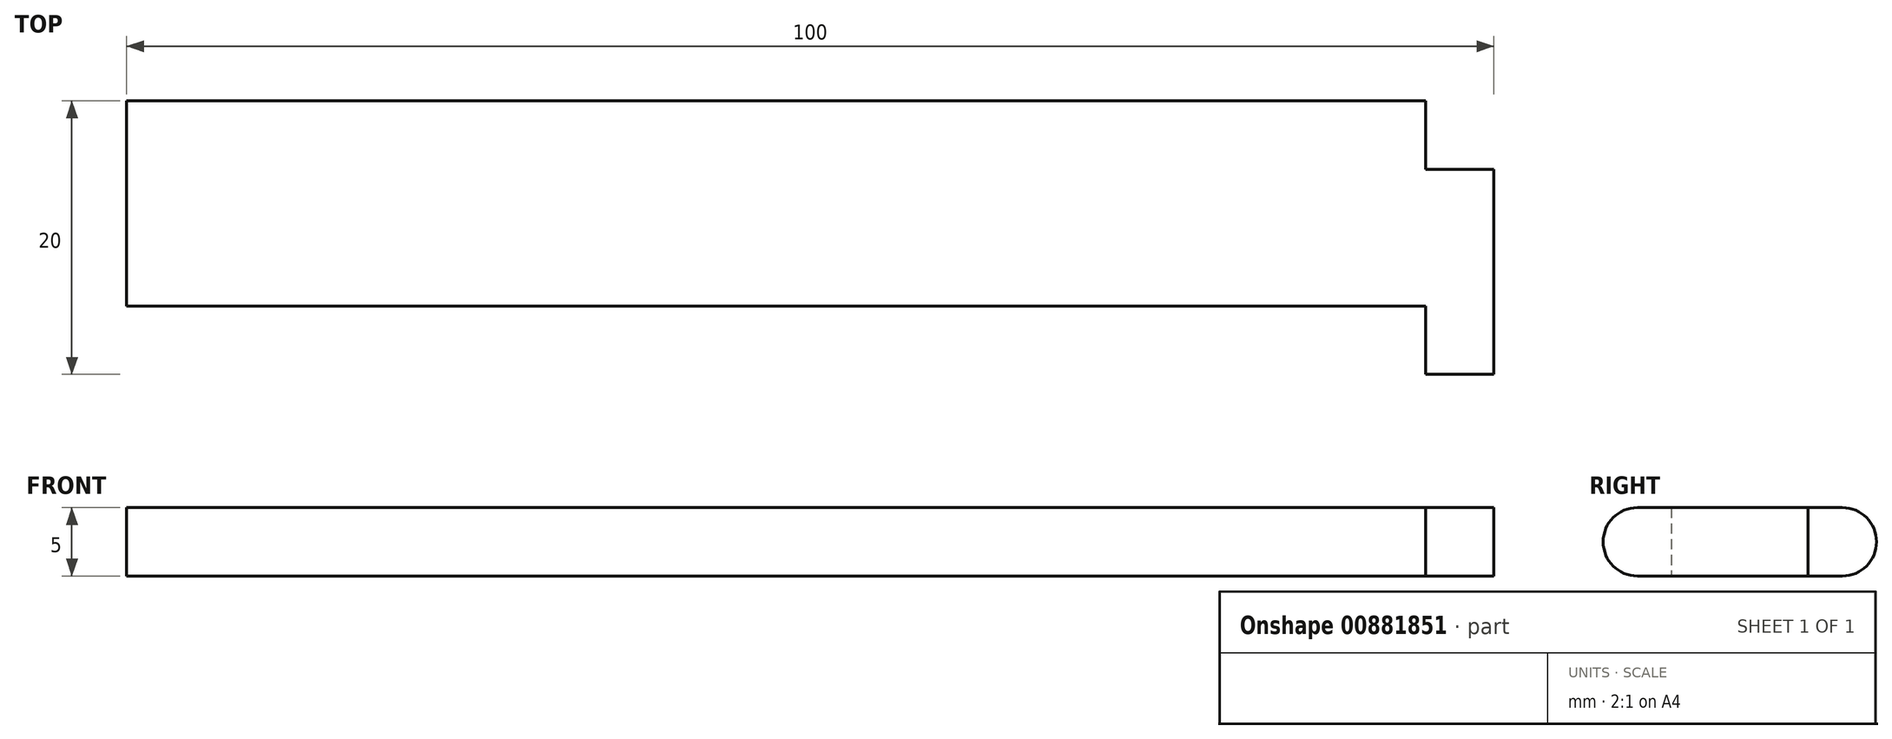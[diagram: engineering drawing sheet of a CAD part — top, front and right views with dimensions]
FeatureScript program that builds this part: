
annotation { "Feature Type Name" : "Feature", "Feature Type Description" : "" }
export const myFeature = defineFeature(function(context is Context, id is Id, definition is map)
    precondition{}
    {
        {
            var Q0;
            Q0=qCreatedBy(makeId("Top.planeOp"),FACE);
            var sketch = newSketch(context, id + "F0", { "sketchPlane" : qUnion([Q0])});
            skLineSegment(sketch, "E0", {"start": v(0, 7.5) * mm, "end": v(95, 7.5) * mm});
            skLineSegment(sketch, "E1", {"start": v(95, 7.5) * mm, "end": v(95, 2.5) * mm});
            skLineSegment(sketch, "E2", {"start": v(95, 2.5) * mm, "end": v(100, 2.5) * mm});
            skLineSegment(sketch, "E3", {"start": v(100, 2.5) * mm, "end": v(100, -12.5) * mm});
            skLineSegment(sketch, "E4", {"start": v(100, -12.5) * mm, "end": v(95, -12.5) * mm});
            skLineSegment(sketch, "E5", {"start": v(95, -12.5) * mm, "end": v(95, -7.5) * mm});
            skLineSegment(sketch, "E6", {"start": v(95, -7.5) * mm, "end": v(0, -7.5) * mm});
            skLineSegment(sketch, "E7", {"start": v(0, -7.5) * mm, "end": v(0, 7.5) * mm});
            skSolve(sketch);
        }
        {
            var Q0;
            Q0=makeQuery(id+"F0.imprint","IMPRINT",FACE,{"disambiguationData":[TD([[makeQuery(id+"F0.imprint","IMPRINT",EDGE,{"derivedFrom":sQuery(id+"F0.wireOp",EDGE,"E0")}),-1.0]])]});
            extrude(context, id + "F1", {"entities" : qUnion([Q0]), "endBound" : BoundingType.SYMMETRIC, "depth" : 5 * mm, "offsetDistance" : 25 * mm});
        }
        {
            var Q0;
            Q0=makeQuery(id+"F1.opExtrude","CAP_EDGE",EDGE,{"disambiguationData":[OSD([sQuery(id+"F0.wireOp",EDGE,"E4")])],"isStart":false});
            var Q1;
            Q1=makeQuery(id+"F1.opExtrude","CAP_EDGE",EDGE,{"disambiguationData":[OSD([sQuery(id+"F0.wireOp",EDGE,"E4")])],"isStart":true});
            var Q2;
            Q2=makeQuery(id+"F1.opExtrude","CAP_EDGE",EDGE,{"disambiguationData":[OSD([sQuery(id+"F0.wireOp",EDGE,"E0")])],"isStart":false});
            var Q3;
            Q3=makeQuery(id+"F1.opExtrude","CAP_EDGE",EDGE,{"disambiguationData":[OSD([sQuery(id+"F0.wireOp",EDGE,"E0")])],"isStart":true});
            fillet(context, id + "F2", {"entities" : qUnion([Q0, Q1, Q2, Q3]), "radius" : 2.5 * mm, "tangentPropagation" : true, "allowEdgeOverflow" : false});
        }
    });
